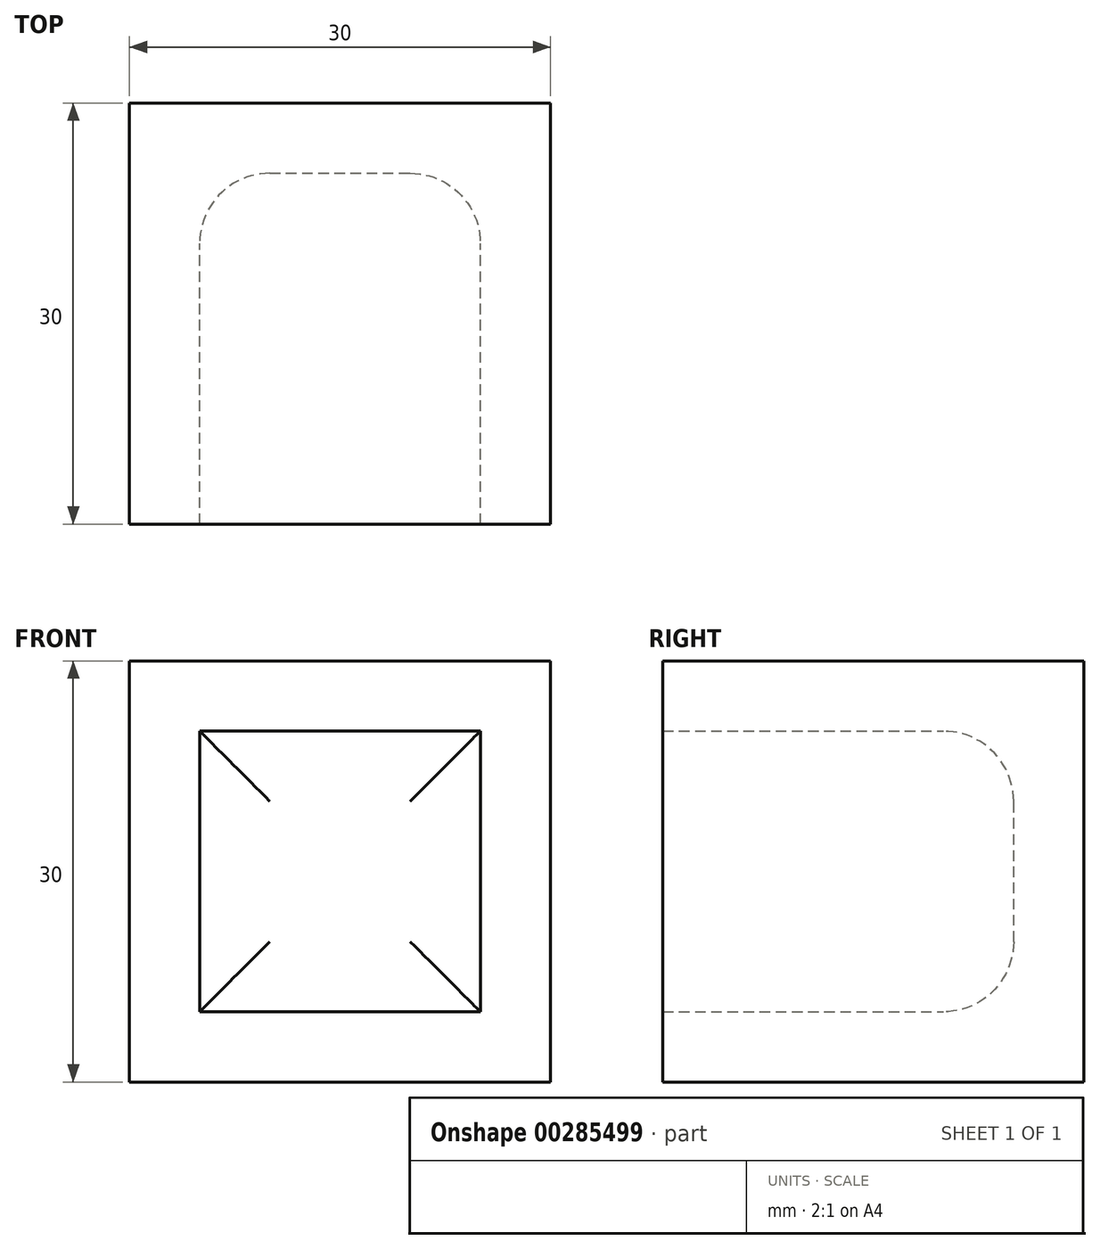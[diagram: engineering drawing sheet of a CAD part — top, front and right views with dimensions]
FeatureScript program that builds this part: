
annotation { "Feature Type Name" : "Feature", "Feature Type Description" : "" }
export const myFeature = defineFeature(function(context is Context, id is Id, definition is map)
    precondition{}
    {
        {
            var Q0;
            Q0=qCreatedBy(makeId("Front.planeOp"),FACE);
            var sketch = newSketch(context, id + "F0", { "sketchPlane" : qUnion([Q0])});
            skLineSegment(sketch, "E0.bottom", {"start": v(0, 0) * mm, "end": v(30, 0) * mm});
            skLineSegment(sketch, "E0.top", {"start": v(0, 30) * mm, "end": v(30, 30) * mm});
            skLineSegment(sketch, "E0.left", {"start": v(0, 0) * mm, "end": v(0, 30) * mm});
            skLineSegment(sketch, "E0.right", {"start": v(30, 0) * mm, "end": v(30, 30) * mm});
            skSolve(sketch);
        }
        {
            var Q0;
            Q0 = qSketchRegion(id + "F0", true);
            extrude(context, id + "F1", {"entities" : qUnion([Q0]), "depth" : 30 * mm});
        }
        {
            var Q0;
            Q0=makeQuery(id+"F1.opExtrude","CAP_FACE",FACE,{"disambiguationData":[OSD([sQuery(id+"F0.wireOp",EDGE,"E0.bottom"),sQuery(id+"F0.wireOp",EDGE,"E0.top"),sQuery(id+"F0.wireOp",EDGE,"E0.left"),sQuery(id+"F0.wireOp",EDGE,"E0.right")])],"isStart":false});
            shell(context, id + "F2", {"entities" : qUnion([Q0]), "thickness" : 5 * mm});
        }
        {
            var Q0;
            Q0=makeQuery(id+"F2.opShell","OFFSET_FACE",FACE,{"disambiguationData":[OSD([sQuery(id+"F0.wireOp",EDGE,"E0.bottom"),sQuery(id+"F0.wireOp",EDGE,"E0.top"),sQuery(id+"F0.wireOp",EDGE,"E0.left"),sQuery(id+"F0.wireOp",EDGE,"E0.right")])]});
            fillet(context, id + "F3", {"entities" : qUnion([Q0]), "radius" : 5 * mm, "tangentPropagation" : true, "allowEdgeOverflow" : false});
        }
    });
